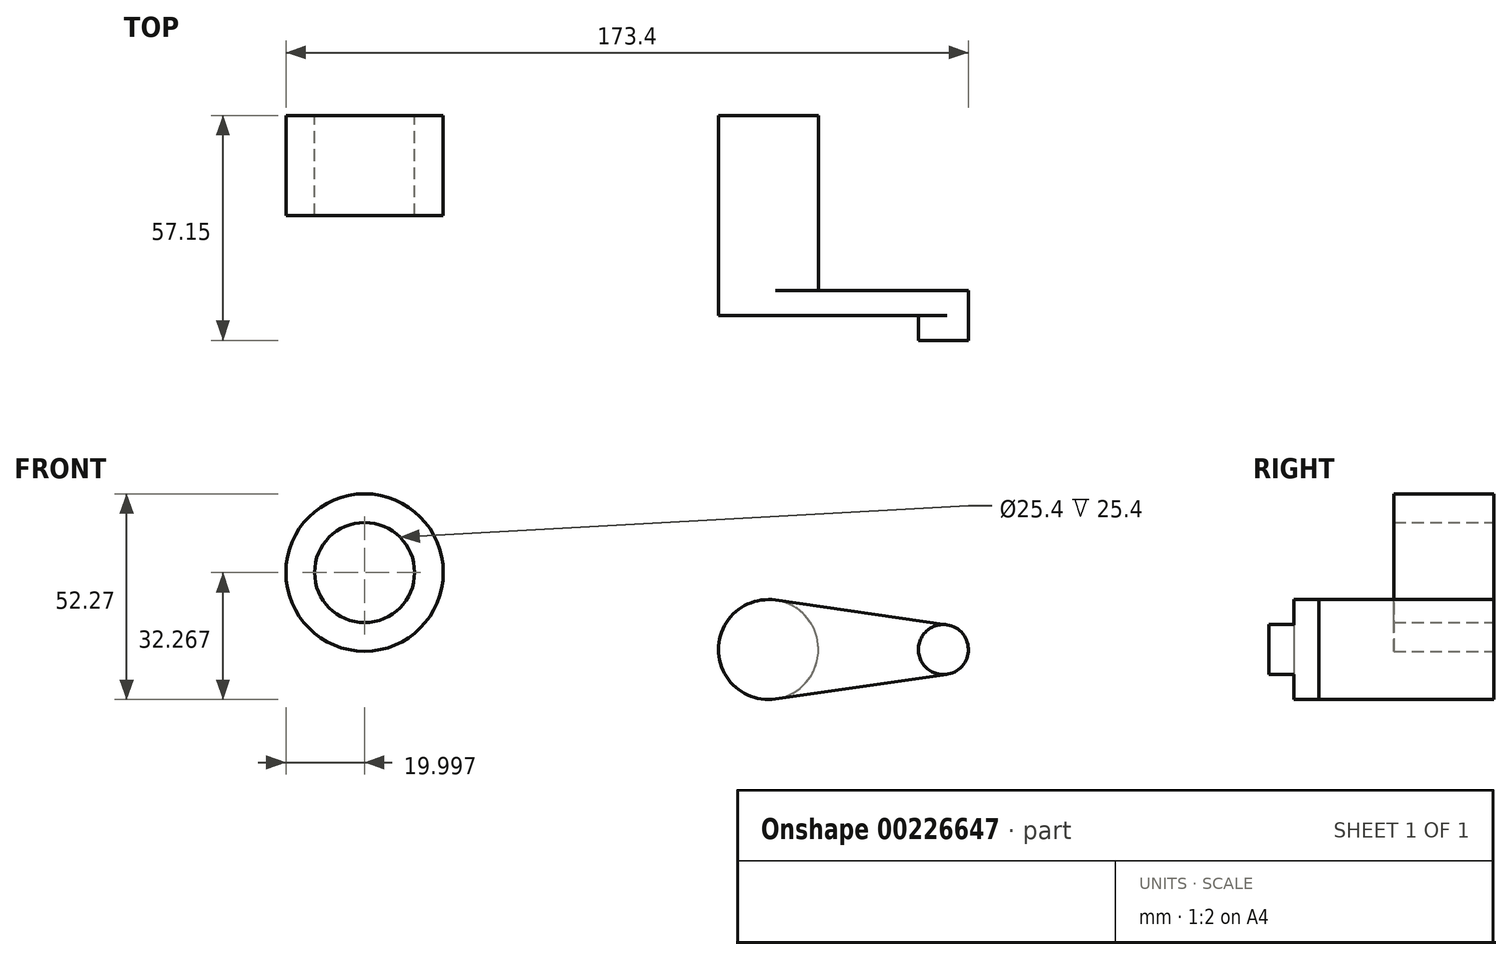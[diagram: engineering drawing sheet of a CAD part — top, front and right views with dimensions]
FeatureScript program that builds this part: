
annotation { "Feature Type Name" : "Feature", "Feature Type Description" : "" }
export const myFeature = defineFeature(function(context is Context, id is Id, definition is map)
    precondition{}
    {
        {
            var Q0;
            Q0=qCreatedBy(makeId("Front.planeOp"),FACE);
            var sketch = newSketch(context, id + "F0", { "sketchPlane" : qUnion([Q0])});
            skCircle(sketch, "E0", {"center": v(0, 0) * mm, "radius": 12.7 * mm});
            skCircle(sketch, "E1", {"center": v(44.45, 0) * mm, "radius": 6.35 * mm});
            skLineSegment(sketch, "E2", {"start": v(12.7, 0) * mm, "end": v(38.1, 0) * mm});
            skLineSegment(sketch, "E3", {"start": v(45.36, 6.28) * mm, "end": v(1.81, 12.57) * mm});
            skLineSegment(sketch, "E4", {"start": v(1.81, -12.57) * mm, "end": v(45.36, -6.28) * mm});
            skSolve(sketch);
        }
        {
            var Q0;
            Q0=makeQuery(id+"F0.imprint","IMPRINT",FACE,{"disambiguationData":[TD([[makeQuery(id+"F0.imprint","IMPRINT",EDGE,{"derivedFrom":sQuery(id+"F0.wireOp",EDGE,"E0")}),1.0]])]});
            extrude(context, id + "F1", {"entities" : qUnion([Q0]), "depth" : 50.8 * mm});
        }
        {
            var Q0;
            {var subQ0=sQuery(id+"F0.wireOp",EDGE,"E2");Q0=makeQuery(id+"F0.imprint","IMPRINT",FACE,{"disambiguationData":[TD([[makeQuery(id+"F0.imprint","IMPRINT",EDGE,{"derivedFrom":subQ0}),1.0]])]});}
            var Q1;
            {var subQ0=sQuery(id+"F0.wireOp",EDGE,"E2");Q1=makeQuery(id+"F0.imprint","IMPRINT",FACE,{"disambiguationData":[TD([[makeQuery(id+"F0.imprint","IMPRINT",EDGE,{"derivedFrom":subQ0}),-1.0]])]});}
            var Q2;
            {var subQ0=sQuery(id+"F0.wireOp",EDGE,"E1");var subQ1=makeQuery(id+"F0.imprint","INTERSECT",VERTEX,{"derivedFrom":[subQ0,sQuery(id+"F0.wireOp",EDGE,"E2")]});Q2=makeQuery(id+"F0.imprint","IMPRINT",FACE,{"disambiguationData":[TD([[makeQuery(id+"F0.imprint","IMPRINT",EDGE,{"disambiguationData":[TD([[subQ1,1.0]])],"derivedFrom":subQ0}),1.0]])]});}
            extrude(context, id + "F2", {"entities" : qUnion([Q0, Q1, Q2]), "operationType" : NewBodyOperationType.ADD, "depth" : 50.8 * mm, "hasSecondDirection" : true, "secondDirectionOppositeDirection" : false, "secondDirectionDepth" : 44.45 * mm});
        }
        {
            var Q0;
            {var subQ0=sQuery(id+"F0.wireOp",EDGE,"E1");var subQ1=makeQuery(id+"F0.imprint","INTERSECT",VERTEX,{"derivedFrom":[subQ0,sQuery(id+"F0.wireOp",EDGE,"E2")]});Q0=makeQuery(id+"F0.imprint","IMPRINT",FACE,{"disambiguationData":[TD([[makeQuery(id+"F0.imprint","IMPRINT",EDGE,{"disambiguationData":[TD([[subQ1,1.0]])],"derivedFrom":subQ0}),1.0]])]});}
            extrude(context, id + "F3", {"entities" : qUnion([Q0]), "operationType" : NewBodyOperationType.ADD, "depth" : 57.15 * mm, "hasSecondDirection" : true, "secondDirectionOppositeDirection" : false, "secondDirectionDepth" : 50.8 * mm});
        }
        {
            var Q0;
            Q0=qCreatedBy(makeId("Front.planeOp"),FACE);
            var sketch = newSketch(context, id + "F4", { "sketchPlane" : qUnion([Q0])});
            skCircle(sketch, "E5", {"center": v(-102.6, 19.57) * mm, "radius": 12.7 * mm});
            skCircle(sketch, "E6", {"center": v(-102.6, 19.57) * mm, "radius": 20 * mm});
            skSolve(sketch);
        }
        {
            var Q0;
            Q0=makeQuery(id+"F4.imprint","IMPRINT",FACE,{"disambiguationData":[TD([[makeQuery(id+"F4.imprint","IMPRINT",EDGE,{"derivedFrom":sQuery(id+"F4.wireOp",EDGE,"E5")}),-1.0]])]});
            extrude(context, id + "F5", {"entities" : qUnion([Q0]), "depth" : 25.4 * mm});
        }
    });
